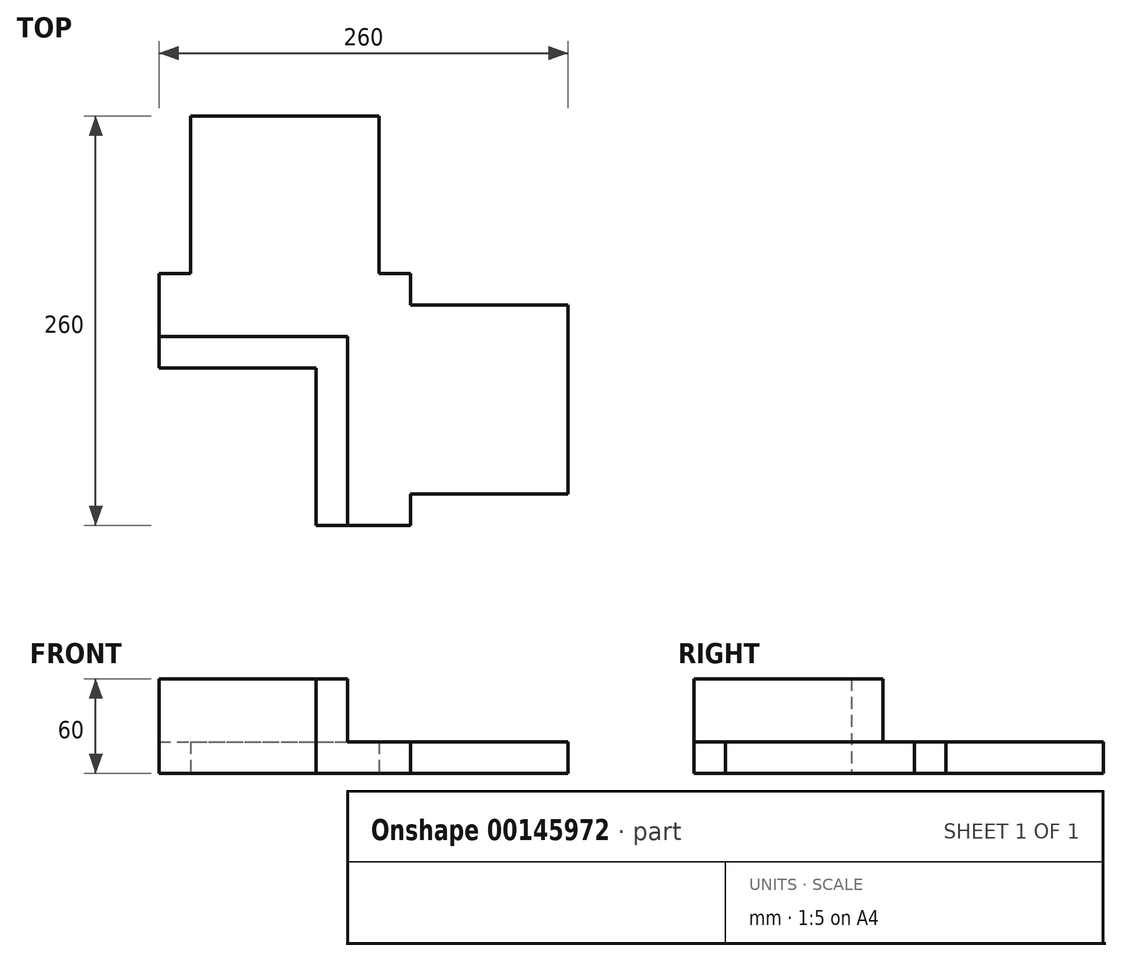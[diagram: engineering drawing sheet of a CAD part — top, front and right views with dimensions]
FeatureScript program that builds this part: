
annotation { "Feature Type Name" : "Feature", "Feature Type Description" : "" }
export const myFeature = defineFeature(function(context is Context, id is Id, definition is map)
    precondition{}
    {
        {
            var Q0;
            Q0=qCreatedBy(makeId("Top.planeOp"),FACE);
            var sketch = newSketch(context, id + "F0", { "sketchPlane" : qUnion([Q0])});
            skLineSegment(sketch, "E0", {"start": v(0, 0) * mm, "end": v(-100, 0) * mm});
            skLineSegment(sketch, "E1", {"start": v(-100, 0) * mm, "end": v(-100, 60) * mm});
            skLineSegment(sketch, "E2", {"start": v(-100, 60) * mm, "end": v(-80, 60) * mm});
            skLineSegment(sketch, "E3", {"start": v(-80, 60) * mm, "end": v(-80, 160) * mm});
            skLineSegment(sketch, "E4", {"start": v(-80, 160) * mm, "end": v(40, 160) * mm});
            skLineSegment(sketch, "E5", {"start": v(40, 160) * mm, "end": v(40, 60) * mm});
            skLineSegment(sketch, "E6", {"start": v(40, 60) * mm, "end": v(60, 60) * mm});
            skLineSegment(sketch, "E7.MirrorCS", {"start": v(60, 40) * mm, "end": v(60, 60) * mm});
            skLineSegment(sketch, "E8.MirrorCS", {"start": v(160, 40) * mm, "end": v(60, 40) * mm});
            skLineSegment(sketch, "E9.MirrorCS", {"start": v(160, -80) * mm, "end": v(160, 40) * mm});
            skLineSegment(sketch, "E10.MirrorCS", {"start": v(60, -80) * mm, "end": v(160, -80) * mm});
            skLineSegment(sketch, "E11.MirrorCS", {"start": v(60, -100) * mm, "end": v(60, -80) * mm});
            skLineSegment(sketch, "E12.MirrorCS", {"start": v(0, -100) * mm, "end": v(60, -100) * mm});
            skLineSegment(sketch, "E13.MirrorCS", {"start": v(0, 0) * mm, "end": v(0, -100) * mm});
            skSolve(sketch);
        }
        {
            var Q0;
            Q0 = qSketchRegion(id + "F0", true);
            extrude(context, id + "F1", {"entities" : qUnion([Q0]), "depth" : 20 * mm});
        }
        {
            var Q0;
            Q0=makeQuery(id+"F1.opExtrude","CAP_FACE",FACE,{"disambiguationData":[OSD([sQuery(id+"F0.wireOp",EDGE,"E0"),sQuery(id+"F0.wireOp",EDGE,"E1"),sQuery(id+"F0.wireOp",EDGE,"E2"),sQuery(id+"F0.wireOp",EDGE,"E3"),sQuery(id+"F0.wireOp",EDGE,"E4"),sQuery(id+"F0.wireOp",EDGE,"E5"),sQuery(id+"F0.wireOp",EDGE,"E6"),sQuery(id+"F0.wireOp",EDGE,"E7.MirrorCS"),sQuery(id+"F0.wireOp",EDGE,"E8.MirrorCS"),sQuery(id+"F0.wireOp",EDGE,"E9.MirrorCS"),sQuery(id+"F0.wireOp",EDGE,"E10.MirrorCS"),sQuery(id+"F0.wireOp",EDGE,"E11.MirrorCS"),sQuery(id+"F0.wireOp",EDGE,"E12.MirrorCS"),sQuery(id+"F0.wireOp",EDGE,"E13.MirrorCS")])],"isStart":false});
            var sketch = newSketch(context, id + "F2", { "sketchPlane" : qUnion([Q0])});
            skLineSegment(sketch, "E14", {"start": v(-100, 0) * mm, "end": v(-100, 20) * mm});
            skLineSegment(sketch, "E15", {"start": v(-100, 20) * mm, "end": v(20, 20) * mm});
            skLineSegment(sketch, "E16", {"start": v(20, 20) * mm, "end": v(20, -100) * mm});
            skLineSegment(sketch, "E17", {"start": v(20, -100) * mm, "end": v(0, -100) * mm});
            skLineSegment(sketch, "E18", {"start": v(0, -100) * mm, "end": v(0, 0) * mm});
            skLineSegment(sketch, "E19", {"start": v(0, 0) * mm, "end": v(-100, 0) * mm});
            skSolve(sketch);
        }
        {
            var Q0;
            Q0 = qSketchRegion(id + "F2", true);
            extrude(context, id + "F3", {"entities" : qUnion([Q0]), "operationType" : NewBodyOperationType.ADD, "depth" : 40 * mm});
        }
    });
